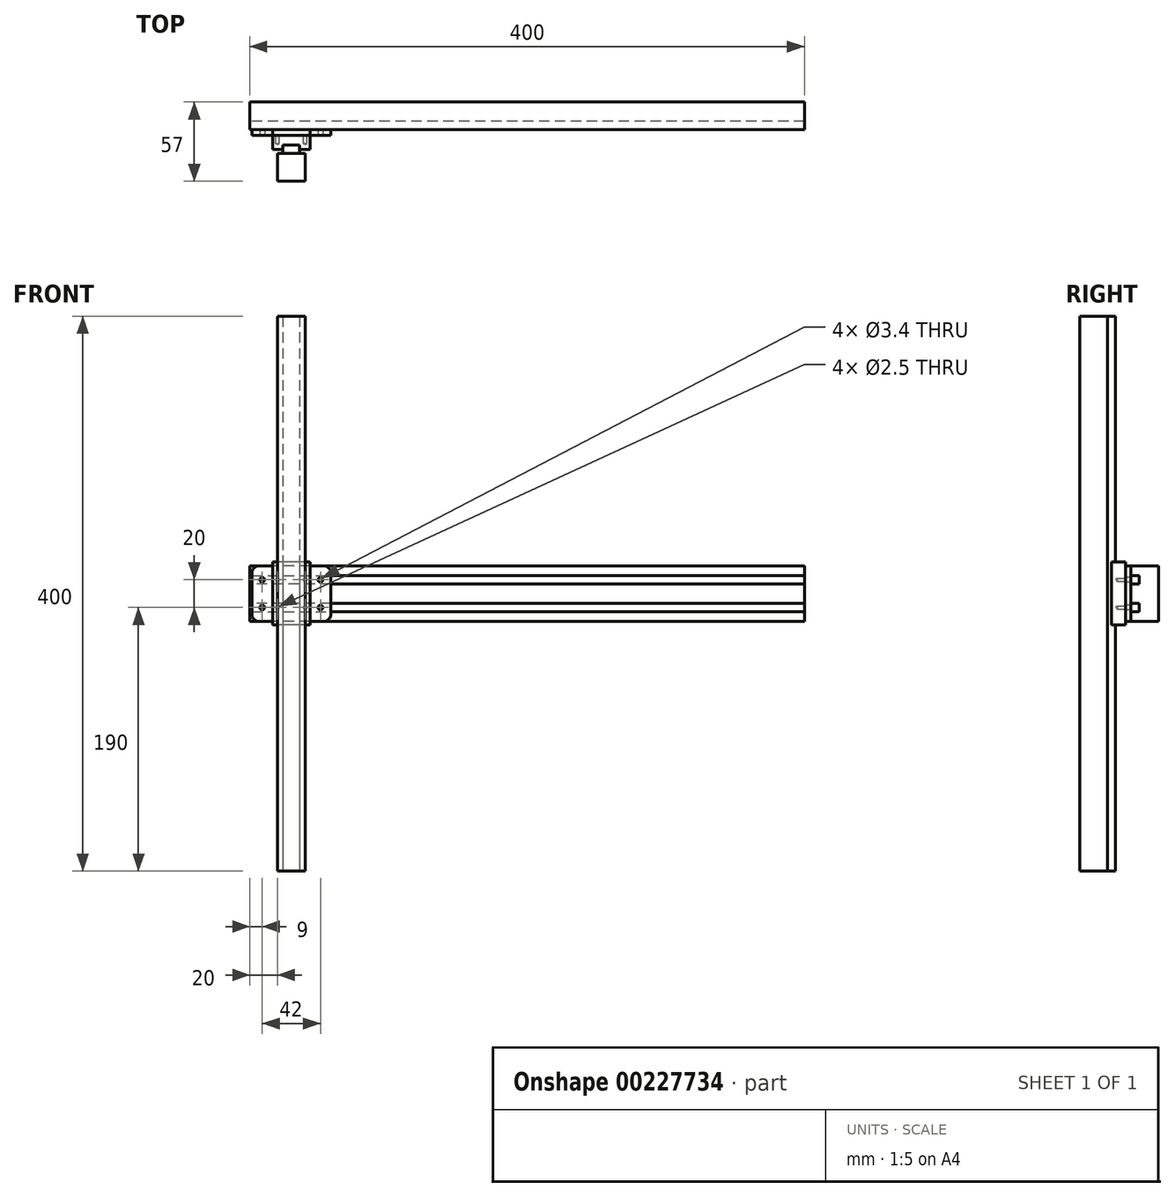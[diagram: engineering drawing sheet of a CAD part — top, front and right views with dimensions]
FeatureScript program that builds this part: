
annotation { "Feature Type Name" : "Feature", "Feature Type Description" : "" }
export const myFeature = defineFeature(function(context is Context, id is Id, definition is map)
    precondition{}
    {
        {
            var Q0;
            Q0=qCreatedBy(makeId("Front.planeOp"),FACE);
            var sketch = newSketch(context, id + "F0", { "sketchPlane" : qUnion([Q0])});
            skLineSegment(sketch, "E0.bottom", {"start": v(200, -20) * mm, "end": v(-200, -20) * mm});
            skLineSegment(sketch, "E0.top", {"start": v(200, 20) * mm, "end": v(-200, 20) * mm});
            skLineSegment(sketch, "E0.left", {"start": v(200, -20) * mm, "end": v(200, 20) * mm});
            skLineSegment(sketch, "E0.right", {"start": v(-200, -20) * mm, "end": v(-200, 20) * mm});
            skPoint(sketch, "E0.middle", {"position": v(0, 0) * mm});
            skSolve(sketch);
        }
        {
            var Q0;
            Q0 = qSketchRegion(id + "F0", true);
            extrude(context, id + "F1", {"entities" : qUnion([Q0]), "oppositeDirection" : true, "depth" : 20 * mm, "offsetDistance" : 25 * mm});
        }
        {
            var Q0;
            Q0=makeQuery(id+"F1.opExtrude","CAP_FACE",FACE,{"disambiguationData":[OSD([sQuery(id+"F0.wireOp",EDGE,"E0.bottom"),sQuery(id+"F0.wireOp",EDGE,"E0.top"),sQuery(id+"F0.wireOp",EDGE,"E0.left"),sQuery(id+"F0.wireOp",EDGE,"E0.right")])],"isStart":true});
            var sketch = newSketch(context, id + "F2", { "sketchPlane" : qUnion([Q0])});
            skLineSegment(sketch, "E1", {"start": v(200, -6.9) * mm, "end": v(-200, -6.9) * mm});
            skLineSegment(sketch, "E2", {"start": v(-200, -13.1) * mm, "end": v(200, -13.1) * mm});
            skLineSegment(sketch, "E3", {"start": v(-200, 0) * mm, "end": v(200, 0) * mm, "construction": true});
            skLineSegment(sketch, "E4.MirrorCS", {"start": v(200, 6.9) * mm, "end": v(-200, 6.9) * mm});
            skLineSegment(sketch, "E5.MirrorCS", {"start": v(-200, 13.1) * mm, "end": v(200, 13.1) * mm});
            skSolve(sketch);
        }
        {
            var Q0;
            {var subQ0=sQuery(id+"F2.wireOp",EDGE,"E4.MirrorCS");Q0=makeQuery(id+"F2.imprint","IMPRINT",FACE,{"disambiguationData":[TD([[makeQuery(id+"F2.imprint","IMPRINT",EDGE,{"derivedFrom":subQ0}),-1.0]])]});}
            var Q1;
            {var subQ0=sQuery(id+"F2.wireOp",EDGE,"E1");Q1=makeQuery(id+"F2.imprint","IMPRINT",FACE,{"disambiguationData":[TD([[makeQuery(id+"F2.imprint","IMPRINT",EDGE,{"derivedFrom":subQ0}),1.0]])]});}
            extrude(context, id + "F3", {"entities" : qUnion([Q0, Q1]), "operationType" : NewBodyOperationType.REMOVE, "oppositeDirection" : true, "depth" : 6.1 * mm, "offsetDistance" : 25 * mm});
        }
        {
            var Q0;
            {var subQ0=sQuery(id+"F0.wireOp",EDGE,"E0.top");var subQ1=sQuery(id+"F0.wireOp",EDGE,"E0.left");var subQ2=sQuery(id+"F0.wireOp",EDGE,"E0.right");Q0=makeQuery(id+"F3.boolean.opBoolean","SPLIT",FACE,{"disambiguationData":[TD([makeQuery(id+"F1.opExtrude","SWEPT_FACE",FACE,{"disambiguationData":[OSD([subQ0])]})])],"derivedFrom":makeQuery(id+"F1.opExtrude","CAP_FACE",FACE,{"disambiguationData":[OSD([sQuery(id+"F0.wireOp",EDGE,"E0.bottom"),subQ0,subQ1,subQ2])],"isStart":true})});}
            cPlane(context, id + "F4", {"entities" : qUnion([Q0]), "cplaneType" : CPlaneType.OFFSET, "offset" : 4 * mm, "width" : 150 * mm, "height" : 150 * mm});
        }
        {
            var Q0;
            Q0=qCreatedBy(id+"F4.planeOp",FACE);
            var sketch = newSketch(context, id + "F5", { "sketchPlane" : qUnion([Q0])});
            skLineSegment(sketch, "E6.bottom", {"start": v(-156.5, -22.7) * mm, "end": v(-183.5, -22.7) * mm});
            skLineSegment(sketch, "E6.top", {"start": v(-156.5, 22.7) * mm, "end": v(-183.5, 22.7) * mm});
            skLineSegment(sketch, "E6.left", {"start": v(-156.5, -22.7) * mm, "end": v(-156.5, 22.7) * mm});
            skLineSegment(sketch, "E6.right", {"start": v(-183.5, -22.7) * mm, "end": v(-183.5, 22.7) * mm});
            skPoint(sketch, "E6.middle", {"position": v(-170, 0) * mm});
            skPoint(sketch, "E7", {"position": v(-180, 10) * mm});
            skPoint(sketch, "E8", {"position": v(-160, 10) * mm});
            skPoint(sketch, "E9", {"position": v(-160, -10) * mm});
            skPoint(sketch, "E10", {"position": v(-180, -10) * mm});
            skLineSegment(sketch, "E11", {"start": v(-180, 10) * mm, "end": v(-160, 10) * mm, "construction": true});
            skPoint(sketch, "E12", {"position": v(-170, 10) * mm});
            skLineSegment(sketch, "E13", {"start": v(-160, 10) * mm, "end": v(-160, -10) * mm, "construction": true});
            skPoint(sketch, "E14", {"position": v(-160, 0) * mm});
            skSolve(sketch);
        }
        {
            var Q0;
            Q0 = qSketchRegion(id + "F5", true);
            extrude(context, id + "F6", {"entities" : qUnion([Q0]), "operationType" : NewBodyOperationType.ADD, "depth" : 10 * mm, "offsetDistance" : 25 * mm});
        }
        {
            var Q0;
            Q0=sQuery(id+"F5.wireOp",VERTEX,"E8");
            var Q1;
            Q1=sQuery(id+"F5.wireOp",VERTEX,"E7");
            var Q2;
            Q2=sQuery(id+"F5.wireOp",VERTEX,"E9");
            var Q3;
            Q3=sQuery(id+"F5.wireOp",VERTEX,"E10");
            var Q4;
            Q4=makeQuery(id+"F6.opExtrude","SWEPT_BODY",BODY,{"disambiguationData":[OSD([sQuery(id+"F5.wireOp",EDGE,"E6.bottom"),sQuery(id+"F5.wireOp",EDGE,"E6.top"),sQuery(id+"F5.wireOp",EDGE,"E6.left"),sQuery(id+"F5.wireOp",EDGE,"E6.right")])]});
            hole(context, id + "F7", {"style" : HoleStyle.SIMPLE, "endStyle" : HoleEndStyle.BLIND, "oppositeDirection" : true, "standardTappedOrClearance" : lookupTablePath({ "standard" : "ISO", "engagement" : "75%", "pitch" : "0.5 mm", "size" : "M3", "type" : "Tapped" }), "standardBlindInLast" : lookupTablePath({ "standard" : "ISO", "fit" : "Normal", "engagement" : "75%", "pitch" : "0.5 mm", "size" : "M3", "type" : "Clearance & tapped" }), "holeDiameter" : 2.5 * mm, "majorDiameter" : 3 * mm, "showTappedDepth" : true, "holeDepth" : 6 * mm, "tappedDepth" : 4.5 * mm, "tapClearance" : 3, "locations" : qUnion([Q0, Q1, Q2, Q3]), "scope" : qUnion([Q4])});
        }
        {
            var Q0;
            Q0=makeQuery(id+"F6.opExtrude","CAP_FACE",FACE,{"disambiguationData":[OSD([sQuery(id+"F5.wireOp",EDGE,"E6.bottom"),sQuery(id+"F5.wireOp",EDGE,"E6.top"),sQuery(id+"F5.wireOp",EDGE,"E6.left"),sQuery(id+"F5.wireOp",EDGE,"E6.right")])],"isStart":true});
            var sketch = newSketch(context, id + "F8", { "sketchPlane" : qUnion([Q0])});
            skPoint(sketch, "E15.0", {"position": v(160, 10) * mm});
            skPoint(sketch, "E16.0", {"position": v(180, 10) * mm});
            skPoint(sketch, "E17.0", {"position": v(160, -10) * mm});
            skPoint(sketch, "E18.0", {"position": v(180, -10) * mm});
            skLineSegment(sketch, "E19.bottom", {"start": v(198.5, -20) * mm, "end": v(141.5, -20) * mm});
            skLineSegment(sketch, "E19.top", {"start": v(198.5, 20) * mm, "end": v(141.5, 20) * mm});
            skLineSegment(sketch, "E19.left", {"start": v(198.5, -20) * mm, "end": v(198.5, 20) * mm});
            skLineSegment(sketch, "E19.right", {"start": v(141.5, -20) * mm, "end": v(141.5, 20) * mm});
            skPoint(sketch, "E19.middle", {"position": v(170, 0) * mm});
            skPoint(sketch, "E20", {"position": v(191, 10) * mm});
            skPoint(sketch, "E21", {"position": v(191, -10) * mm});
            skLineSegment(sketch, "E22", {"start": v(198.5, -10) * mm, "end": v(183.5, -10) * mm, "construction": true});
            skLineSegment(sketch, "E23", {"start": v(170, 7.22) * mm, "end": v(170, -7.85) * mm, "construction": true});
            skPoint(sketch, "E24.MirrorP", {"position": v(149, 10) * mm});
            skPoint(sketch, "E25.MirrorP", {"position": v(149, -10) * mm});
            skSolve(sketch);
        }
        {
            var Q0;
            Q0=makeQuery(id+"F8.imprint","IMPRINT",FACE,{"disambiguationData":[TD([[makeQuery(id+"F8.imprint","IMPRINT",EDGE,{"derivedFrom":makeQuery(id+"F7.hole-0.boolean.opBoolean","COPY",EDGE,{"derivedFrom":makeQuery(id+"F7.hole-0.opRevolve","SWEPT_EDGE",EDGE,{"disambiguationData":[OSD([sQuery(id+"F7.hole-0.sketch.wireOp",EDGE,"core_line_2"),sQuery(id+"F7.hole-0.sketch.wireOp",EDGE,"core_line_3")])]})})}),-1.0]])]});
            var Q1;
            {var subQ0=sQuery(id+"F8.wireOp",EDGE,"E19.right");Q1=makeQuery(id+"F8.imprint","IMPRINT",FACE,{"disambiguationData":[TD([[makeQuery(id+"F8.imprint","IMPRINT",EDGE,{"derivedFrom":subQ0}),-1.0]])]});}
            var Q2;
            {var subQ0=sQuery(id+"F8.wireOp",EDGE,"E19.left");Q2=makeQuery(id+"F8.imprint","IMPRINT",FACE,{"disambiguationData":[TD([[makeQuery(id+"F8.imprint","IMPRINT",EDGE,{"derivedFrom":subQ0}),1.0]])]});}
            var Q3;
            Q3=makeQuery(id+"F8.imprint","IMPRINT",FACE,{"disambiguationData":[TD([[makeQuery(id+"F8.imprint","IMPRINT",EDGE,{"derivedFrom":makeQuery(id+"F7.hole-0.boolean.opBoolean","COPY",EDGE,{"derivedFrom":makeQuery(id+"F7.hole-0.opRevolve","SWEPT_EDGE",EDGE,{"disambiguationData":[OSD([sQuery(id+"F7.hole-0.sketch.wireOp",EDGE,"core_line_2"),sQuery(id+"F7.hole-0.sketch.wireOp",EDGE,"core_line_3")])]})})}),1.0]])]});
            var Q4;
            Q4=makeQuery(id+"F8.imprint","IMPRINT",FACE,{"disambiguationData":[TD([[makeQuery(id+"F8.imprint","IMPRINT",EDGE,{"derivedFrom":makeQuery(id+"F7.hole-2.boolean.opBoolean","COPY",EDGE,{"derivedFrom":makeQuery(id+"F7.hole-2.opRevolve","SWEPT_EDGE",EDGE,{"disambiguationData":[OSD([sQuery(id+"F7.hole-2.sketch.wireOp",EDGE,"core_line_2"),sQuery(id+"F7.hole-2.sketch.wireOp",EDGE,"core_line_3")])]})})}),1.0]])]});
            var Q5;
            Q5=makeQuery(id+"F8.imprint","IMPRINT",FACE,{"disambiguationData":[TD([[makeQuery(id+"F8.imprint","IMPRINT",EDGE,{"derivedFrom":makeQuery(id+"F7.hole-1.boolean.opBoolean","COPY",EDGE,{"derivedFrom":makeQuery(id+"F7.hole-1.opRevolve","SWEPT_EDGE",EDGE,{"disambiguationData":[OSD([sQuery(id+"F7.hole-1.sketch.wireOp",EDGE,"core_line_2"),sQuery(id+"F7.hole-1.sketch.wireOp",EDGE,"core_line_3")])]})})}),1.0]])]});
            var Q6;
            Q6=makeQuery(id+"F8.imprint","IMPRINT",FACE,{"disambiguationData":[TD([[makeQuery(id+"F8.imprint","IMPRINT",EDGE,{"derivedFrom":makeQuery(id+"F7.hole-3.boolean.opBoolean","COPY",EDGE,{"derivedFrom":makeQuery(id+"F7.hole-3.opRevolve","SWEPT_EDGE",EDGE,{"disambiguationData":[OSD([sQuery(id+"F7.hole-3.sketch.wireOp",EDGE,"core_line_2"),sQuery(id+"F7.hole-3.sketch.wireOp",EDGE,"core_line_3")])]})})}),1.0]])]});
            extrude(context, id + "F9", {"entities" : qUnion([Q0, Q1, Q2, Q3, Q4, Q5, Q6]), "depth" : 4 * mm, "offsetDistance" : 25 * mm});
        }
        {
            var Q0;
            Q0=makeQuery(id+"F9.opExtrude","CAP_FACE",FACE,{"disambiguationData":[OSD([sQuery(id+"F8.wireOp",EDGE,"E19.bottom"),sQuery(id+"F8.wireOp",EDGE,"E19.top"),sQuery(id+"F8.wireOp",EDGE,"E19.left"),sQuery(id+"F8.wireOp",EDGE,"E19.right")])],"isStart":false});
            var sketch = newSketch(context, id + "F10", { "sketchPlane" : qUnion([Q0])});
            skPoint(sketch, "E26.0", {"position": v(160, 10) * mm});
            skPoint(sketch, "E27.0", {"position": v(180, 10) * mm});
            skPoint(sketch, "E28.0", {"position": v(160, -10) * mm});
            skPoint(sketch, "E29.0", {"position": v(180, -10) * mm});
            skSolve(sketch);
        }
        {
            var Q0;
            Q0=sQuery(id+"F10.wireOp",VERTEX,"E26.0");
            var Q1;
            Q1=sQuery(id+"F10.wireOp",VERTEX,"E27.0");
            var Q2;
            Q2=sQuery(id+"F10.wireOp",VERTEX,"E28.0");
            var Q3;
            Q3=sQuery(id+"F10.wireOp",VERTEX,"E29.0");
            var Q4;
            Q4=makeQuery(id+"F9.opExtrude","SWEPT_BODY",BODY,{"disambiguationData":[OSD([sQuery(id+"F8.wireOp",EDGE,"E19.bottom"),sQuery(id+"F8.wireOp",EDGE,"E19.top"),sQuery(id+"F8.wireOp",EDGE,"E19.left"),sQuery(id+"F8.wireOp",EDGE,"E19.right")])]});
            hole(context, id + "F11", {"style" : HoleStyle.C_SINK, "endStyle" : HoleEndStyle.THROUGH, "standardTappedOrClearance" : lookupTablePath({ "fit" : "Normal", "standard" : "ISO", "size" : "M3", "type" : "Clearance" }), "standardBlindInLast" : lookupTablePath({ "fit" : "Normal", "standard" : "ISO", "engagement" : "75%", "pitch" : "0.5 mm", "size" : "M3", "type" : "Clearance & tapped" }), "holeDiameter" : 3.4 * mm, "cSinkDiameter" : 6.72 * mm, "cSinkAngle" : 90 * degree, "majorDiameter" : 3 * mm, "isTappedThrough" : true, "tappedDepth" : 4.5 * mm, "tapClearance" : 3, "locations" : qUnion([Q0, Q1, Q2, Q3]), "scope" : qUnion([Q4])});
        }
        {
            var Q0;
            Q0=sQuery(id+"F8.wireOp",VERTEX,"E20");
            var Q1;
            Q1=sQuery(id+"F8.wireOp",VERTEX,"E21");
            var Q2;
            Q2=sQuery(id+"F8.wireOp",VERTEX,"E24.MirrorP");
            var Q3;
            Q3=sQuery(id+"F8.wireOp",VERTEX,"E25.MirrorP");
            var Q4;
            Q4=makeQuery(id+"F9.opExtrude","SWEPT_BODY",BODY,{"disambiguationData":[OSD([sQuery(id+"F8.wireOp",EDGE,"E19.bottom"),sQuery(id+"F8.wireOp",EDGE,"E19.top"),sQuery(id+"F8.wireOp",EDGE,"E19.left"),sQuery(id+"F8.wireOp",EDGE,"E19.right")])]});
            hole(context, id + "F12", {"style" : HoleStyle.SIMPLE, "endStyle" : HoleEndStyle.THROUGH, "oppositeDirection" : true, "standardTappedOrClearance" : lookupTablePath({ "fit" : "Normal", "standard" : "ISO", "size" : "M3", "type" : "Clearance" }), "standardBlindInLast" : lookupTablePath({ "fit" : "Normal", "standard" : "ISO", "engagement" : "75%", "pitch" : "0.5 mm", "size" : "M3", "type" : "Clearance & tapped" }), "holeDiameter" : 3.4 * mm, "majorDiameter" : 5 * mm, "isTappedThrough" : true, "tappedDepth" : 4.5 * mm, "tapClearance" : 3, "locations" : qUnion([Q0, Q1, Q2, Q3]), "scope" : qUnion([Q4])});
        }
        {
            var Q0;
            Q0=makeQuery(id+"F9.opExtrude","SWEPT_EDGE",EDGE,{"disambiguationData":[OSD([sQuery(id+"F8.wireOp",EDGE,"E19.top"),sQuery(id+"F8.wireOp",EDGE,"E19.left")])]});
            var Q1;
            Q1=makeQuery(id+"F9.opExtrude","SWEPT_EDGE",EDGE,{"disambiguationData":[OSD([sQuery(id+"F8.wireOp",EDGE,"E19.top"),sQuery(id+"F8.wireOp",EDGE,"E19.right")])]});
            var Q2;
            Q2=makeQuery(id+"F9.opExtrude","SWEPT_EDGE",EDGE,{"disambiguationData":[OSD([sQuery(id+"F8.wireOp",EDGE,"E19.bottom"),sQuery(id+"F8.wireOp",EDGE,"E19.left")])]});
            var Q3;
            Q3=makeQuery(id+"F9.opExtrude","SWEPT_EDGE",EDGE,{"disambiguationData":[OSD([sQuery(id+"F8.wireOp",EDGE,"E19.bottom"),sQuery(id+"F8.wireOp",EDGE,"E19.right")])]});
            fillet(context, id + "F13", {"entities" : qUnion([Q0, Q1, Q2, Q3]), "tangentPropagation" : true, "radius" : 5 * mm, "defaultsChanged" : false, "vertexSettings" : [], "allowEdgeOverflow" : false});
        }
        {
            var Q0;
            Q0=makeQuery(id+"F6.opExtrude","SWEPT_FACE",FACE,{"disambiguationData":[OSD([sQuery(id+"F5.wireOp",EDGE,"E6.top")])]});
            var sketch = newSketch(context, id + "F14", { "sketchPlane" : qUnion([Q0])});
            skLineSegment(sketch, "E30.bottom", {"start": v(-164, -17) * mm, "end": v(-176, -17) * mm});
            skLineSegment(sketch, "E30.top", {"start": v(-164, -11) * mm, "end": v(-176, -11) * mm});
            skLineSegment(sketch, "E30.left", {"start": v(-164, -17) * mm, "end": v(-164, -11) * mm});
            skLineSegment(sketch, "E30.right", {"start": v(-176, -17) * mm, "end": v(-176, -11) * mm});
            skPoint(sketch, "E30.middle", {"position": v(-170, -14) * mm});
            skSolve(sketch);
        }
        {
            var Q0;
            {var subQ0=sQuery(id+"F14.wireOp",EDGE,"E30.bottom");Q0=makeQuery(id+"F14.imprint","IMPRINT",FACE,{"disambiguationData":[TD([[makeQuery(id+"F14.imprint","IMPRINT",EDGE,{"derivedFrom":subQ0}),-1.0]])]});}
            var Q1;
            {var subQ0=sQuery(id+"F14.wireOp",EDGE,"E30.top");Q1=makeQuery(id+"F14.imprint","IMPRINT",FACE,{"disambiguationData":[TD([[makeQuery(id+"F14.imprint","IMPRINT",EDGE,{"derivedFrom":subQ0}),1.0]])]});}
            var Q2;
            Q2=makeQuery(id+"F6.opExtrude","SWEPT_FACE",FACE,{"disambiguationData":[OSD([sQuery(id+"F5.wireOp",EDGE,"E6.bottom")])]});
            extrude(context, id + "F15", {"entities" : qUnion([Q0, Q1]), "operationType" : NewBodyOperationType.ADD, "depth" : (200 - (45.4 / 2)) * mm, "endBoundEntityFace" : qUnion([Q2]), "offsetDistance" : 25 * mm, "hasSecondDirection" : true, "secondDirectionOppositeDirection" : true, "secondDirectionDepth" : (200 + (45.4 / 2)) * mm});
        }
        {
            var Q0;
            Q0=makeQuery(id+"F15.opExtrude","SWEPT_FACE",FACE,{"disambiguationData":[OSD([sQuery(id+"F14.wireOp",EDGE,"E30.bottom")])]});
            var sketch = newSketch(context, id + "F16", { "sketchPlane" : qUnion([Q0])});
            skLineSegment(sketch, "E31.bottom", {"start": v(-160, -200) * mm, "end": v(-180, -200) * mm});
            skLineSegment(sketch, "E31.top", {"start": v(-160, 200) * mm, "end": v(-180, 200) * mm});
            skLineSegment(sketch, "E31.left", {"start": v(-160, -200) * mm, "end": v(-160, 200) * mm});
            skLineSegment(sketch, "E31.right", {"start": v(-180, -200) * mm, "end": v(-180, 200) * mm});
            skPoint(sketch, "E31.middle", {"position": v(-170, 0) * mm});
            skPoint(sketch, "E31.middle.positionSnap0", {"position": v(-176, 0) * mm});
            skPoint(sketch, "E31.centerSnap0", {"position": v(-176, 0) * mm});
            skLineSegment(sketch, "E32", {"start": v(-176, 0) * mm, "end": v(-164, 0) * mm, "construction": true});
            skSolve(sketch);
        }
        {
            var Q0;
            Q0 = qSketchRegion(id + "F16", true);
            extrude(context, id + "F17", {"entities" : qUnion([Q0]), "depth" : 20 * mm, "offsetDistance" : 25 * mm});
        }
    });
